# Revit family: Domotics-DomesticRanges-GEWISS-SYSTEM_BOX_WALL-MOUNTING_COMPACT
name_source: partatom
category: Apparecchi elettrici
revit_build: Autodesk Revit 2016 (Build: 20161004_0715(x64)
units: mm (PartAtom-declared; Revit-internal decimal feet)

## family parameters
Condiviso = Sì
Host = Superficie
Mantenere orientamento annotazione = No
Punto di calcolo locali = Sì
Quota connettore circolare = Usa diametro
Taglio con vuoti quando caricato = No
Tipo di parte = Normale

## types (1)
- Domotics-DomesticRanges-GEWISS-SYSTEM_BOX_WALL-MOUNTING_COMPACT
    Catalogue = DOMOTICS
    Catalogue Range = SYSTEM - BOXES
    Characteristics = Halogen free
    Colour = Cloud white
    Descrizione = COMPACT SURFACE BOX FOR 6 GANG PLATES
    EAN code = 8011564001824
    Electrocod = 0110
    For conduits max Ã˜ (mm) = 16 - 20 - 25
    For trunking dim. (mm) = 14x8.5 30x13 20x10
    Glow Wire Test = 650°C
    IDF = 39974ab4-4bc9-485a-a143-8a4326c98be9
    IDT = f6d0d6ab-408c-4b7e-8fa0-9f8f8c405203
    Immagine tipo = GW24007.jpg
    Modello = GW24007
    Produttore = GEWISS S.p.A.
    Prospetto di default = 1219 mm
    S3P = No
    S6P = Sì
    SEO = Box
    Suitable for = 3+3 gang COMPACT
    Suitable for plates = 3+3 gang
    Technical sheet = https://www.gewiss.com
    Thermo-pressure with ball = 70
    Tipo = System Scatole Parete x Placche Compact_GENERICO : GW24007 Scatola 6 posti da parete compact
    URL = https://www.gewiss.com
    Version file RFA = 19.4

note: source unit labels omitted for Thermo-pressure with ball — the stored unit's dimension contradicts the parameter name (converter mislabeling)
